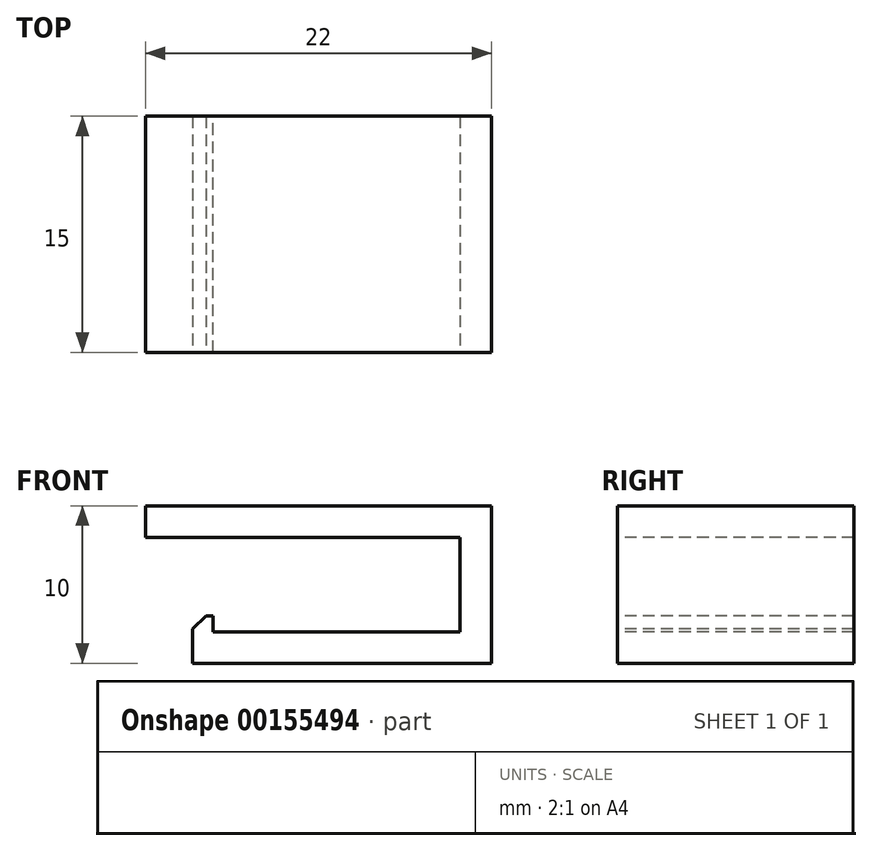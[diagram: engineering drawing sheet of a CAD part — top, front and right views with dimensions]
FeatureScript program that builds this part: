
annotation { "Feature Type Name" : "Feature", "Feature Type Description" : "" }
export const myFeature = defineFeature(function(context is Context, id is Id, definition is map)
    precondition{}
    {
        {
            var Q0;
            Q0=qCreatedBy(makeId("Top.planeOp"),FACE);
            var sketch = newSketch(context, id + "F0", { "sketchPlane" : qUnion([Q0])});
            skLineSegment(sketch, "E0.bottom", {"start": v(-9.5, 7.5) * mm, "end": v(9.5, 7.5) * mm});
            skLineSegment(sketch, "E0.top", {"start": v(-9.5, -7.5) * mm, "end": v(9.5, -7.5) * mm});
            skLineSegment(sketch, "E0.left", {"start": v(-9.5, 7.5) * mm, "end": v(-9.5, -7.5) * mm});
            skLineSegment(sketch, "E0.right", {"start": v(9.5, 7.5) * mm, "end": v(9.5, -7.5) * mm});
            skPoint(sketch, "E0.middle", {"position": v(0, 0) * mm});
            skSolve(sketch);
        }
        {
            var Q0;
            Q0=makeQuery(id+"F0.imprint","IMPRINT",FACE,{"disambiguationData":[TD([[makeQuery(id+"F0.imprint","IMPRINT",EDGE,{"derivedFrom":sQuery(id+"F0.wireOp",EDGE,"E0.bottom")}),-1.0]])]});
            extrude(context, id + "F1", {"entities" : qUnion([Q0]), "depth" : 2 * mm});
        }
        {
            var Q0;
            Q0=makeQuery(id+"F1.opExtrude","CAP_FACE",FACE,{"disambiguationData":[OSD([sQuery(id+"F0.wireOp",EDGE,"E0.bottom"),sQuery(id+"F0.wireOp",EDGE,"E0.top"),sQuery(id+"F0.wireOp",EDGE,"E0.left"),sQuery(id+"F0.wireOp",EDGE,"E0.right")])],"isStart":false});
            var sketch = newSketch(context, id + "F2", { "sketchPlane" : qUnion([Q0])});
            skLineSegment(sketch, "E1", {"start": v(7.5, 7.5) * mm, "end": v(7.5, -7.5) * mm});
            skSolve(sketch);
        }
        {
            var Q0;
            {var subQ0=sQuery(id+"F2.wireOp",EDGE,"E1");Q0=makeQuery(id+"F2.imprint","IMPRINT",FACE,{"disambiguationData":[TD([[makeQuery(id+"F2.imprint","IMPRINT",EDGE,{"derivedFrom":subQ0}),1.0]])]});}
            extrude(context, id + "F3", {"entities" : qUnion([Q0]), "operationType" : NewBodyOperationType.ADD, "depth" : 8 * mm});
        }
        {
            var Q0;
            Q0=makeQuery(id+"F3.opExtrude","SWEPT_FACE",FACE,{"disambiguationData":[OSD([sQuery(id+"F2.wireOp",EDGE,"E1")])]});
            var sketch = newSketch(context, id + "F4", { "sketchPlane" : qUnion([Q0])});
            skLineSegment(sketch, "E2", {"start": v(-7.5, 8) * mm, "end": v(7.5, 8) * mm});
            skSolve(sketch);
        }
        {
            var Q0;
            {var subQ0=sQuery(id+"F4.wireOp",EDGE,"E2");Q0=makeQuery(id+"F4.imprint","IMPRINT",FACE,{"disambiguationData":[TD([[makeQuery(id+"F4.imprint","IMPRINT",EDGE,{"derivedFrom":subQ0}),1.0]])]});}
            extrude(context, id + "F5", {"entities" : qUnion([Q0]), "operationType" : NewBodyOperationType.ADD, "depth" : 20 * mm});
        }
        {
            var Q0;
            Q0=makeQuery(id+"F1.opExtrude","CAP_FACE",FACE,{"disambiguationData":[OSD([sQuery(id+"F0.wireOp",EDGE,"E0.bottom"),sQuery(id+"F0.wireOp",EDGE,"E0.top"),sQuery(id+"F0.wireOp",EDGE,"E0.left"),sQuery(id+"F0.wireOp",EDGE,"E0.right")])],"isStart":false});
            var sketch = newSketch(context, id + "F6", { "sketchPlane" : qUnion([Q0])});
            skLineSegment(sketch, "E3", {"start": v(-8.2, -7.5) * mm, "end": v(-8.2, 7.5) * mm});
            skSolve(sketch);
        }
        {
            var Q0;
            {var subQ0=sQuery(id+"F6.wireOp",EDGE,"E3");Q0=makeQuery(id+"F6.imprint","IMPRINT",FACE,{"disambiguationData":[TD([[makeQuery(id+"F6.imprint","IMPRINT",EDGE,{"derivedFrom":subQ0}),1.0]])]});}
            extrude(context, id + "F7", {"entities" : qUnion([Q0]), "operationType" : NewBodyOperationType.ADD, "depth" : 1 * mm});
        }
        {
            var Q0;
            {var subQ0=sQuery(id+"F0.wireOp",EDGE,"E0.top");Q0=makeQuery(id+"F7.boolean.opBoolean","MERGE",FACE,{"derivedFrom":[makeQuery(id+"F5.boolean.opBoolean","MERGE",FACE,{"derivedFrom":[makeQuery(id+"F3.boolean.opBoolean","MERGE",FACE,{"derivedFrom":[makeQuery(id+"F1.opExtrude","SWEPT_FACE",FACE,{"disambiguationData":[OSD([subQ0])]}),makeQuery(id+"F3.opExtrude","SWEPT_FACE",FACE,{"disambiguationData":[OSD([subQ0])]})]}),makeQuery(id+"F5.opExtrude","SWEPT_FACE",FACE,{"disambiguationData":[OSD([subQ0,sQuery(id+"F2.wireOp",EDGE,"E1")])]})]}),makeQuery(id+"F7.opExtrude","SWEPT_FACE",FACE,{"disambiguationData":[OSD([subQ0])]})]});}
            var sketch = newSketch(context, id + "F8", { "sketchPlane" : qUnion([Q0])});
            skLineSegment(sketch, "E4", {"start": v(-9.5, 2.2) * mm, "end": v(-8.63, 3) * mm});
            skPoint(sketch, "E5", {"position": v(-8.85, 3) * mm});
            skSolve(sketch);
        }
        {
            var Q0;
            Q0 = qSketchRegion(id + "F8", true);
            var Q1;
            {var subQ0=sQuery(id+"F8.wireOp",EDGE,"E4");Q1=makeQuery(id+"F8.imprint","IMPRINT",FACE,{"disambiguationData":[TD([[makeQuery(id+"F8.imprint","IMPRINT",EDGE,{"derivedFrom":subQ0}),1.0]])]});}
            extrude(context, id + "F9", {"entities" : qUnion([Q0, Q1]), "operationType" : NewBodyOperationType.REMOVE, "oppositeDirection" : true, "depth" : 25 * mm});
        }
    });
